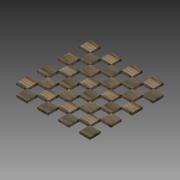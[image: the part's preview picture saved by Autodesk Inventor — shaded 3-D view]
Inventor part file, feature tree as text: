
AUTODESK INVENTOR PART (.ipt)
format: ipt  version: 2015 SP1 (Build 190203100, 203)  size: 239,104 bytes
history: native  units: mm
features: extrude x2, sketch x2
ambient origin geometry x8: Origin, YZ Plane, XZ Plane, XY Plane, X Axis, Y Axis, Z Axis, Center Point
bodies: Solid1 (feature_tree)
feature tree (4):
  extrude  "Extrusion1"  Depth=360.0mm
  extrude  "Extrusion2"  Depth=45.0mm
  sketch  "Sketch1"  dims[d0=360.0mm d1=360.0mm]
  sketch  "Sketch2"  dims[d2=10.0mm d3=0.0mm d4=45.0mm d5=45.0mm d6=40.0mm d8=90.0mm d9=40.0mm d11=90.0mm d15=40.0mm d17=40.0mm d18=45.0mm d19=45.0mm d20=90.0mm d21=90.0mm d22=10.0mm d23=0.0mm]
